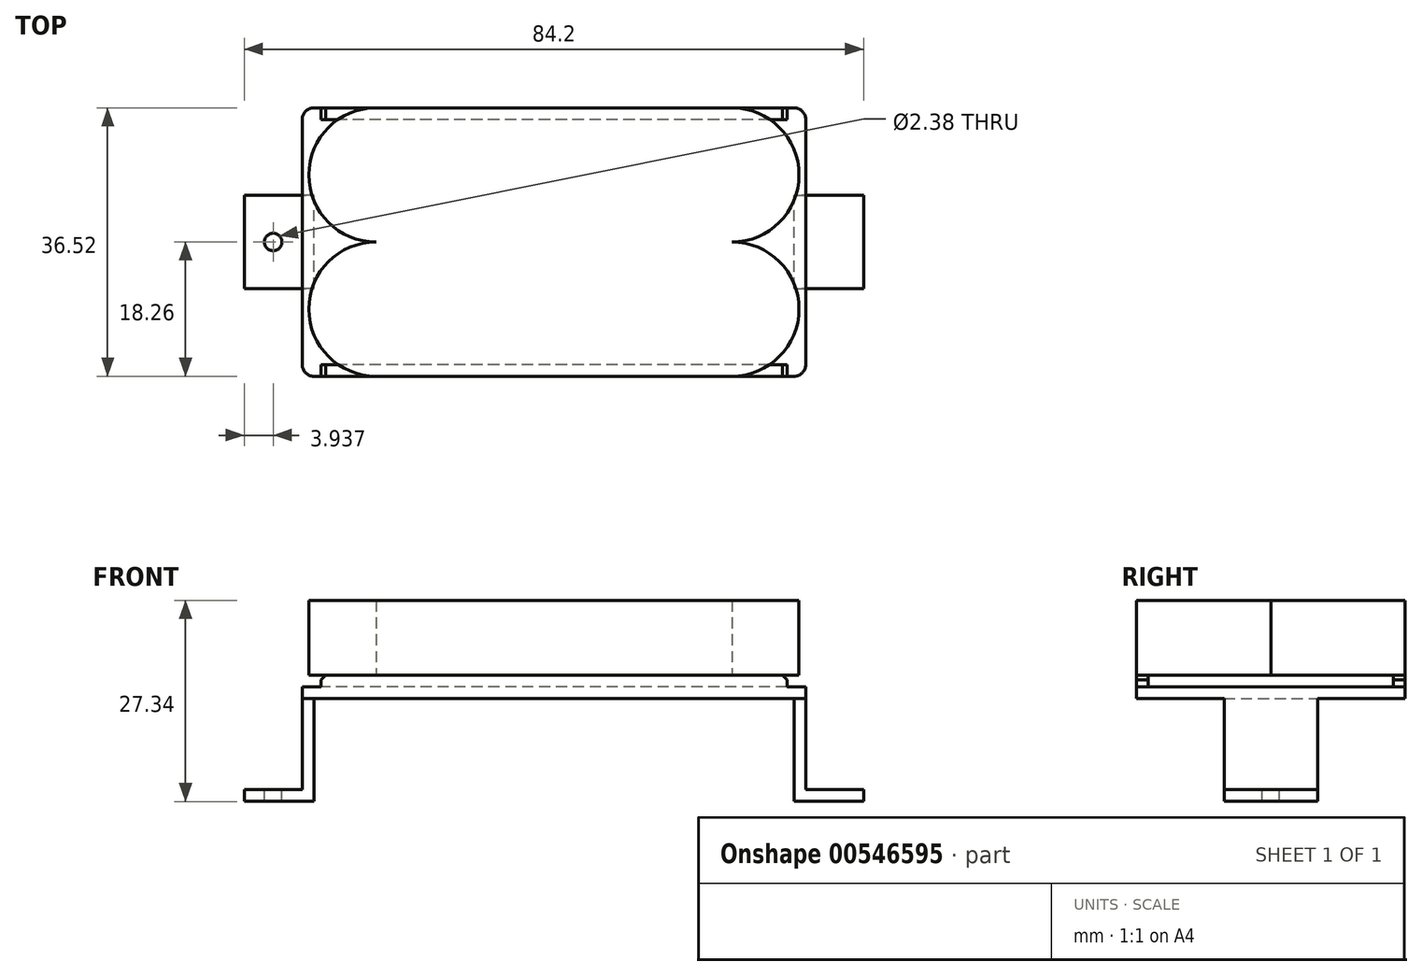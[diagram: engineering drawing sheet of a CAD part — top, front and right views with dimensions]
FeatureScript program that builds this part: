
annotation { "Feature Type Name" : "Feature", "Feature Type Description" : "" }
export const myFeature = defineFeature(function(context is Context, id is Id, definition is map)
    precondition{}
    {
        {
            var Q0;
            Q0=qCreatedBy(makeId("Top.planeOp"),FACE);
            var sketch = newSketch(context, id + "F0", { "sketchPlane" : qUnion([Q0])});
            skLineSegment(sketch, "E0", {"start": v(0, 0) * mm, "end": v(-24.2, 0) * mm});
            skArc(sketch, "E1", {"start": v(-24.2, 0) * mm, "mid": v(-33.32, -9.12) * mm, "end": v(-24.2, -18.25) * mm});
            skLineSegment(sketch, "E2", {"start": v(-24.2, -18.25) * mm, "end": v(24.2, -18.25) * mm});
            skArc(sketch, "E3", {"start": v(24.2, -18.25) * mm, "mid": v(33.32, -9.12) * mm, "end": v(24.2, 0) * mm});
            skLineSegment(sketch, "E4", {"start": v(0, 0) * mm, "end": v(24.2, 0) * mm});
            skLineSegment(sketch, "E5", {"start": v(-33.32, -9.12) * mm, "end": v(33.32, -9.12) * mm});
            skSolve(sketch);
        }
        {
            var Q0;
            {var subQ0=sQuery(id+"F0.wireOp",EDGE,"E2");Q0=makeQuery(id+"F0.imprint","IMPRINT",FACE,{"disambiguationData":[TD([[makeQuery(id+"F0.imprint","IMPRINT",EDGE,{"derivedFrom":subQ0}),1.0]])]});}
            var Q1;
            {var subQ2=sQuery(id+"F0.wireOp",EDGE,"E0");Q1=makeQuery(id+"F0.imprint","IMPRINT",FACE,{"disambiguationData":[TD([[makeQuery(id+"F0.imprint","IMPRINT",EDGE,{"derivedFrom":subQ2}),1.0]])]});}
            extrude(context, id + "F1", {"entities" : qUnion([Q0, Q1]), "depth" : 10.2 * mm});
        }
        {
            var Q0;
            Q0=makeQuery(id+"F1.opExtrude","SWEPT_BODY",BODY,{"disambiguationData":[OSD([sQuery(id+"F0.wireOp",EDGE,"E0"),sQuery(id+"F0.wireOp",EDGE,"E1"),sQuery(id+"F0.wireOp",EDGE,"E2"),sQuery(id+"F0.wireOp",EDGE,"E3"),sQuery(id+"F0.wireOp",EDGE,"E4")])]});
            var Q1;
            Q1=qCreatedBy(makeId("Front.planeOp"),FACE);
            mirror(context, id + "F2", {"operationType" : NewBodyOperationType.ADD, "entities" : qUnion([Q0]), "mirrorPlane" : qUnion([Q1])});
        }
        {
            var Q0;
            Q0=qCreatedBy(makeId("Right.planeOp"),FACE);
            var sketch = newSketch(context, id + "F3", { "sketchPlane" : qUnion([Q0])});
            skLineSegment(sketch, "E6", {"start": v(-18.26, 0) * mm, "end": v(-18.26, -3.18) * mm});
            skLineSegment(sketch, "E7", {"start": v(-18.26, 0) * mm, "end": v(-16.68, 0) * mm});
            skLineSegment(sketch, "E8", {"start": v(-16.68, 0) * mm, "end": v(-16.68, -1.59) * mm});
            skLineSegment(sketch, "E9", {"start": v(-16.68, -1.59) * mm, "end": v(0, -1.59) * mm});
            skLineSegment(sketch, "E10", {"start": v(0, -1.59) * mm, "end": v(0, -3.17) * mm});
            skLineSegment(sketch, "E11", {"start": v(0, -3.17) * mm, "end": v(-18.26, -3.18) * mm});
            skLineSegment(sketch, "E12", {"start": v(0, -3.17) * mm, "end": v(18.26, -3.17) * mm});
            skLineSegment(sketch, "E13", {"start": v(18.26, -3.17) * mm, "end": v(18.26, 0) * mm});
            skLineSegment(sketch, "E14", {"start": v(18.26, 0) * mm, "end": v(16.68, 0) * mm});
            skLineSegment(sketch, "E15", {"start": v(16.68, 0) * mm, "end": v(16.68, -1.59) * mm});
            skLineSegment(sketch, "E16", {"start": v(16.68, -1.59) * mm, "end": v(0, -1.59) * mm});
            skSolve(sketch);
        }
        {
            var Q0;
            Q0=makeQuery(id+"F3.imprint","IMPRINT",FACE,{"disambiguationData":[TD([[makeQuery(id+"F3.imprint","IMPRINT",EDGE,{"derivedFrom":sQuery(id+"F3.wireOp",EDGE,"E6")}),1.0]])]});
            var Q1;
            Q1=makeQuery(id+"F3.imprint","IMPRINT",FACE,{"disambiguationData":[TD([[makeQuery(id+"F3.imprint","IMPRINT",EDGE,{"derivedFrom":sQuery(id+"F3.wireOp",EDGE,"E10")}),1.0]])]});
            extrude(context, id + "F4", {"entities" : qUnion([Q0, Q1]), "operationType" : NewBodyOperationType.ADD, "depth" : 68.45 * mm, "symmetric" : true});
        }
        {
            var Q0;
            Q0=makeQuery(id+"F4.opExtrude","SWEPT_FACE",FACE,{"disambiguationData":[OSD([sQuery(id+"F3.wireOp",EDGE,"E6")])]});
            var sketch = newSketch(context, id + "F5", { "sketchPlane" : qUnion([Q0])});
            skLineSegment(sketch, "E17", {"start": v(-34.23, -1.59) * mm, "end": v(-31.69, -1.59) * mm});
            skLineSegment(sketch, "E18", {"start": v(-31.69, -1.59) * mm, "end": v(-31.69, -0.63) * mm});
            skLineSegment(sketch, "E19", {"start": v(-31.69, -0.63) * mm, "end": v(-31.05, 0) * mm});
            skLineSegment(sketch, "E20", {"start": v(-31.05, 0) * mm, "end": v(-34.23, 0) * mm});
            skLineSegment(sketch, "E21", {"start": v(-34.23, 0) * mm, "end": v(-34.23, -1.59) * mm});
            skLineSegment(sketch, "E22", {"start": v(0, 0) * mm, "end": v(0, -3.18) * mm});
            skLineSegment(sketch, "E23.MirrorCS", {"start": v(31.69, -1.59) * mm, "end": v(31.69, -0.63) * mm});
            skLineSegment(sketch, "E24.MirrorCS", {"start": v(31.69, -0.63) * mm, "end": v(31.05, 0) * mm});
            skLineSegment(sketch, "E25.MirrorCS", {"start": v(31.05, 0) * mm, "end": v(34.23, 0) * mm});
            skLineSegment(sketch, "E26.MirrorCS", {"start": v(34.23, 0) * mm, "end": v(34.23, -1.59) * mm});
            skLineSegment(sketch, "E27.MirrorCS", {"start": v(34.23, -1.59) * mm, "end": v(31.69, -1.59) * mm});
            skSolve(sketch);
        }
        {
            var Q0;
            Q0=makeQuery(id+"F5.imprint","IMPRINT",FACE,{"disambiguationData":[TD([[makeQuery(id+"F5.imprint","IMPRINT",EDGE,{"derivedFrom":sQuery(id+"F5.wireOp",EDGE,"E17")}),1.0]])]});
            var Q1;
            Q1=makeQuery(id+"F5.imprint","IMPRINT",FACE,{"disambiguationData":[TD([[makeQuery(id+"F5.imprint","IMPRINT",EDGE,{"derivedFrom":sQuery(id+"F5.wireOp",EDGE,"E23.MirrorCS")}),-1.0]])]});
            extrude(context, id + "F6", {"entities" : qUnion([Q0, Q1]), "operationType" : NewBodyOperationType.REMOVE, "endBound" : BoundingType.THROUGH_ALL, "oppositeDirection" : true, "depth" : 25.4 * mm});
        }
        {
            var Q0;
            Q0=makeQuery(id+"F4.opExtrude","CAP_EDGE",EDGE,{"disambiguationData":[OSD([sQuery(id+"F3.wireOp",EDGE,"E6")])],"isStart":true});
            var Q1;
            Q1=makeQuery(id+"F4.opExtrude","CAP_EDGE",EDGE,{"disambiguationData":[OSD([sQuery(id+"F3.wireOp",EDGE,"E13")])],"isStart":true});
            var Q2;
            Q2=makeQuery(id+"F4.opExtrude","CAP_EDGE",EDGE,{"disambiguationData":[OSD([sQuery(id+"F3.wireOp",EDGE,"E6")])],"isStart":false});
            var Q3;
            Q3=makeQuery(id+"F4.opExtrude","CAP_EDGE",EDGE,{"disambiguationData":[OSD([sQuery(id+"F3.wireOp",EDGE,"E13")])],"isStart":false});
            fillet(context, id + "F7", {"entities" : qUnion([Q0, Q1, Q2, Q3]), "radius" : 1.59 * mm, "tangentPropagation" : true, "allowEdgeOverflow" : false});
        }
        {
            var Q0;
            Q0=qCreatedBy(makeId("Front.planeOp"),FACE);
            var sketch = newSketch(context, id + "F8", { "sketchPlane" : qUnion([Q0])});
            skLineSegment(sketch, "E28", {"start": v(-34.23, -3.18) * mm, "end": v(-34.23, -15.56) * mm});
            skLineSegment(sketch, "E29", {"start": v(-34.23, -15.56) * mm, "end": v(-42.1, -15.56) * mm});
            skLineSegment(sketch, "E30", {"start": v(-42.1, -15.56) * mm, "end": v(-42.1, -17.15) * mm});
            skLineSegment(sketch, "E31", {"start": v(-42.1, -17.15) * mm, "end": v(-32.64, -17.14) * mm});
            skLineSegment(sketch, "E32", {"start": v(-32.64, -17.14) * mm, "end": v(-32.64, -3.18) * mm});
            skLineSegment(sketch, "E33", {"start": v(-32.64, -3.18) * mm, "end": v(-34.23, -3.18) * mm});
            skLineSegment(sketch, "E34", {"start": v(0, 0) * mm, "end": v(0, -9.8) * mm});
            skLineSegment(sketch, "E35.MirrorCS", {"start": v(32.64, -17.14) * mm, "end": v(32.64, -3.18) * mm});
            skLineSegment(sketch, "E36.MirrorCS", {"start": v(34.23, -3.18) * mm, "end": v(34.23, -15.56) * mm});
            skLineSegment(sketch, "E37.MirrorCS", {"start": v(42.1, -17.15) * mm, "end": v(32.64, -17.14) * mm});
            skLineSegment(sketch, "E38.MirrorCS", {"start": v(34.23, -15.56) * mm, "end": v(42.1, -15.56) * mm});
            skLineSegment(sketch, "E39.MirrorCS", {"start": v(42.1, -15.56) * mm, "end": v(42.1, -17.15) * mm});
            skLineSegment(sketch, "E40.MirrorCS", {"start": v(32.64, -3.18) * mm, "end": v(34.23, -3.18) * mm});
            skSolve(sketch);
        }
        {
            var Q0;
            Q0=makeQuery(id+"F8.imprint","IMPRINT",FACE,{"disambiguationData":[TD([[makeQuery(id+"F8.imprint","IMPRINT",EDGE,{"derivedFrom":sQuery(id+"F8.wireOp",EDGE,"E28")}),1.0]])]});
            var Q1;
            Q1=makeQuery(id+"F8.imprint","IMPRINT",FACE,{"disambiguationData":[TD([[makeQuery(id+"F8.imprint","IMPRINT",EDGE,{"derivedFrom":sQuery(id+"F8.wireOp",EDGE,"E35.MirrorCS")}),-1.0]])]});
            extrude(context, id + "F9", {"entities" : qUnion([Q0, Q1]), "operationType" : NewBodyOperationType.ADD, "depth" : 12.7 * mm, "symmetric" : true});
        }
        {
            var Q0;
            Q0=makeQuery(id+"F9.opExtrude","SWEPT_FACE",FACE,{"disambiguationData":[OSD([sQuery(id+"F8.wireOp",EDGE,"E29")])]});
            var sketch = newSketch(context, id + "F10", { "sketchPlane" : qUnion([Q0])});
            skCircle(sketch, "E41", {"center": v(-38.16, 0) * mm, "radius": 1.2 * mm});
            skLineSegment(sketch, "E42", {"start": v(-42.1, 0) * mm, "end": v(-38.16, 0) * mm});
            skLineSegment(sketch, "E43", {"start": v(-34.23, 0) * mm, "end": v(-38.16, 0) * mm});
            skLineSegment(sketch, "E44", {"start": v(0, 0) * mm, "end": v(0, -9.74) * mm});
            skCircle(sketch, "E45.MirrorC", {"center": v(38.16, 0) * mm, "radius": 1.2 * mm});
            skSolve(sketch);
        }
        {
            var Q0;
            {var subQ0=sQuery(id+"F10.wireOp",EDGE,"E42");var subQ1=sQuery(id+"F10.wireOp",EDGE,"E41");var subQ2=makeQuery(id+"F10.imprint","INTERSECT",VERTEX,{"derivedFrom":[subQ1,subQ0]});Q0=makeQuery(id+"F10.imprint","IMPRINT",FACE,{"disambiguationData":[TD([[makeQuery(id+"F10.imprint","IMPRINT",EDGE,{"disambiguationData":[TD([[subQ2,-1.0]])],"derivedFrom":subQ1}),1.0]])]});}
            var Q1;
            {var subQ0=sQuery(id+"F10.wireOp",EDGE,"E42");var subQ1=sQuery(id+"F10.wireOp",EDGE,"E41");var subQ2=makeQuery(id+"F10.imprint","INTERSECT",VERTEX,{"derivedFrom":[subQ1,subQ0]});Q1=makeQuery(id+"F10.imprint","IMPRINT",FACE,{"disambiguationData":[TD([[makeQuery(id+"F10.imprint","IMPRINT",EDGE,{"disambiguationData":[TD([[subQ2,1.0]])],"derivedFrom":subQ1}),1.0]])]});}
            var Q2;
            Q2=makeQuery(id+"F10.imprint","IMPRINT",FACE,{"disambiguationData":[TD([[makeQuery(id+"F10.imprint","IMPRINT",EDGE,{"derivedFrom":sQuery(id+"F10.wireOp",EDGE,"E45.MirrorC")}),-1.0]])]});
            extrude(context, id + "F11", {"entities" : qUnion([Q0, Q1, Q2]), "operationType" : NewBodyOperationType.REMOVE, "endBound" : BoundingType.THROUGH_ALL, "oppositeDirection" : true, "depth" : 25.4 * mm});
        }
    });
